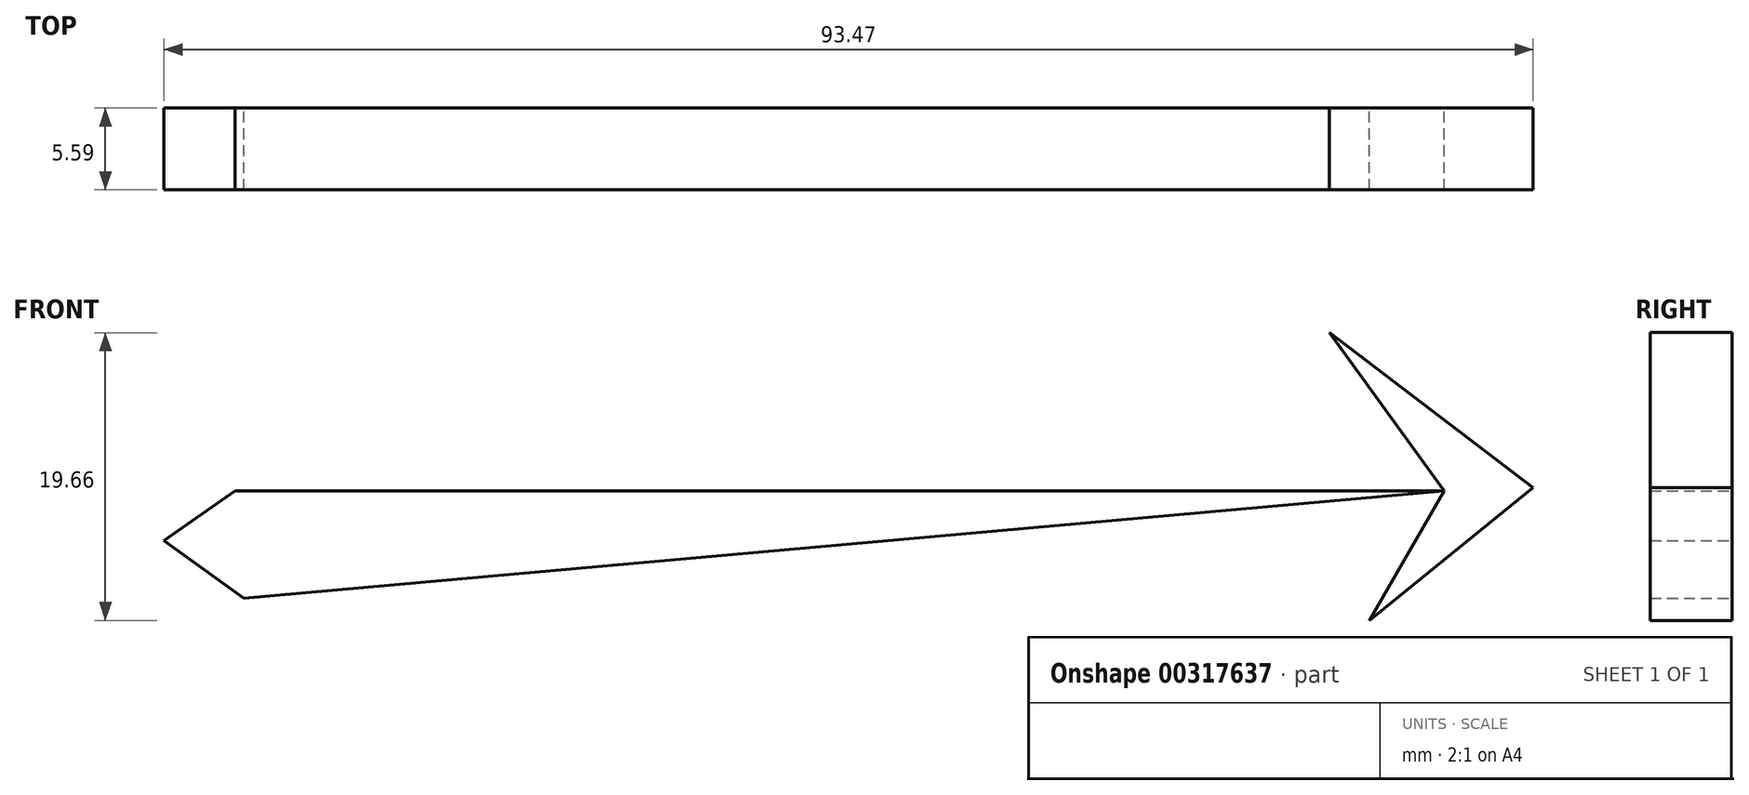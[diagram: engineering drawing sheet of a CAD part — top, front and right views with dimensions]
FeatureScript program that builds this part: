
annotation { "Feature Type Name" : "Feature", "Feature Type Description" : "" }
export const myFeature = defineFeature(function(context is Context, id is Id, definition is map)
    precondition{}
    {
        {
            var Q0;
            Q0=qCreatedBy(makeId("Front.planeOp"),FACE);
            var sketch = newSketch(context, id + "F0", { "sketchPlane" : qUnion([Q0])});
            skLineSegment(sketch, "E0", {"start": v(-40.53, 22.54) * mm, "end": v(52.94, 26.17) * mm});
            skLineSegment(sketch, "E1", {"start": v(52.94, 26.17) * mm, "end": v(39.02, 36.75) * mm});
            skLineSegment(sketch, "E2", {"start": v(39.02, 36.75) * mm, "end": v(46.88, 25.93) * mm});
            skLineSegment(sketch, "E3", {"start": v(46.88, 25.93) * mm, "end": v(41.74, 17.1) * mm});
            skLineSegment(sketch, "E4", {"start": v(41.74, 17.1) * mm, "end": v(52.94, 26.17) * mm});
            skLineSegment(sketch, "E5", {"start": v(46.88, 25.93) * mm, "end": v(-35.7, 25.93) * mm});
            skLineSegment(sketch, "E6", {"start": v(-35.7, 25.93) * mm, "end": v(-40.53, 22.54) * mm});
            skLineSegment(sketch, "E7", {"start": v(-35.09, 18.6) * mm, "end": v(-40.53, 22.54) * mm});
            skLineSegment(sketch, "E8", {"start": v(-35.09, 18.6) * mm, "end": v(46.88, 25.93) * mm});
            skSolve(sketch);
        }
        {
            var Q0;
            Q0 = qSketchRegion(id + "F0", true);
            extrude(context, id + "F1", {"entities" : qUnion([Q0]), "depth" : 5.6 * mm});
        }
    });
